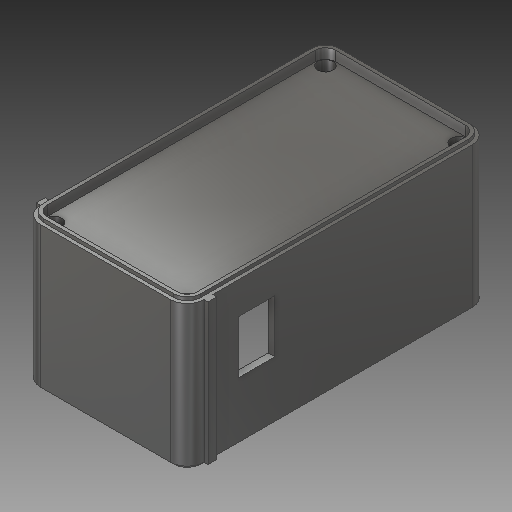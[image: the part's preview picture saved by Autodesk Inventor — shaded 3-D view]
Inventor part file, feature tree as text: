
AUTODESK INVENTOR PART (.ipt)
format: ipt  version: 2018 (Build 220112000, 112)  size: 206,336 bytes
history: mixed  units: in
note: dims shown in document units (in); Inventor stores cm internally (conversion verified against a paired STEP export)
features: mirror x1, imported_body x1
ambient origin geometry x8: Origin, YZ Plane, XZ Plane, XY Plane, X Axis, Y Axis, Z Axis, Center Point
bodies: Solid1 (imported_parasolid)
feature tree (2):
  mirror  "Simetría4"
  imported_body  NMx_Import_Brep_tag  [imported B-rep: ~97 faces, bbox_mm=[25.7, 22.0, 45.0]]
